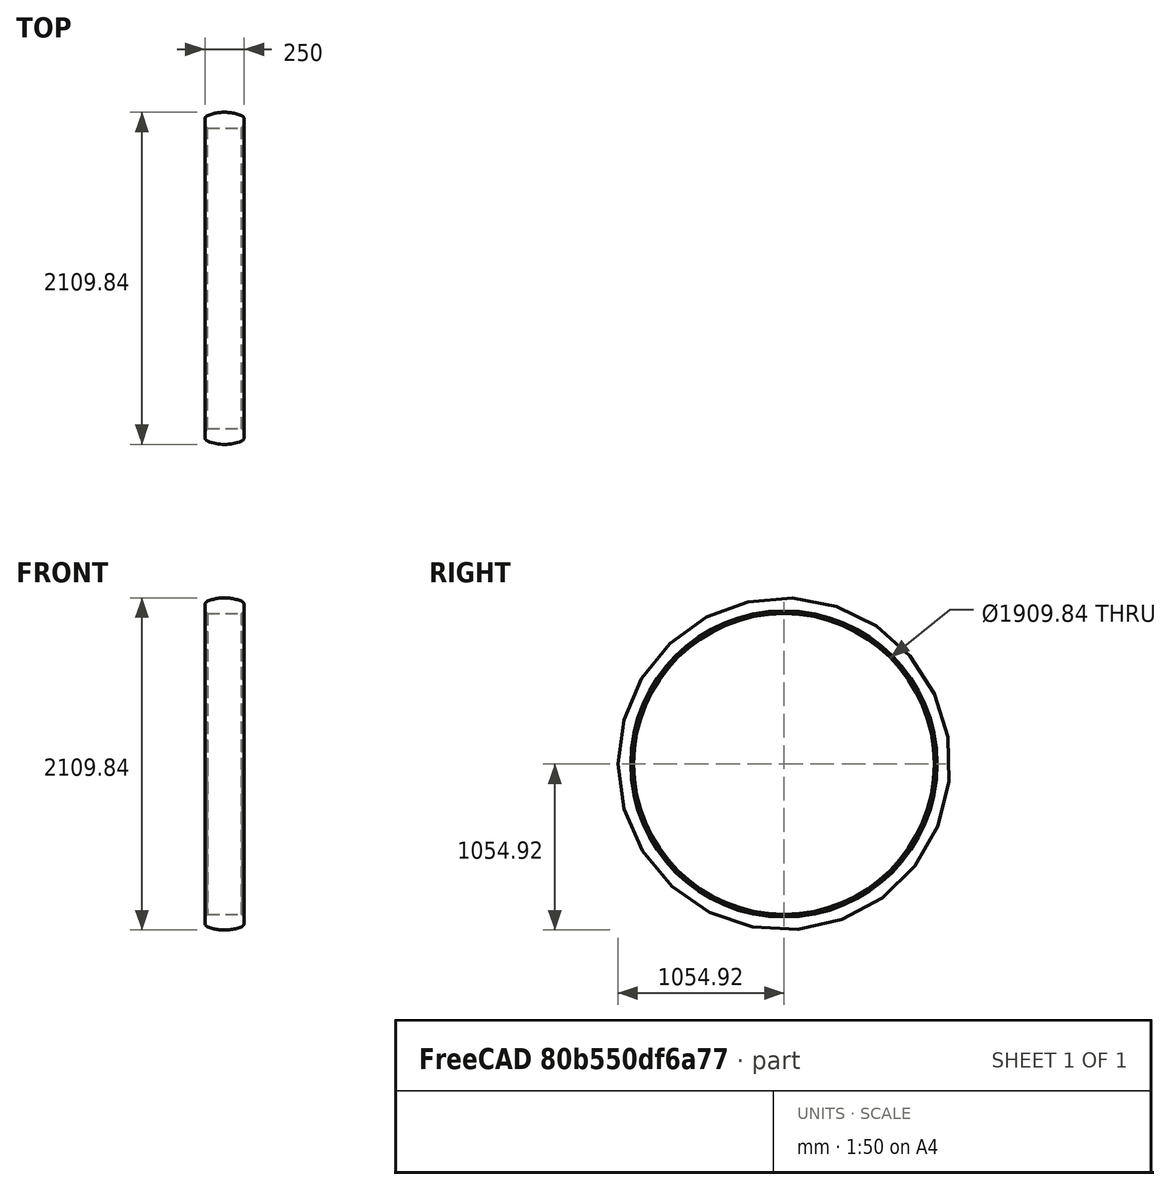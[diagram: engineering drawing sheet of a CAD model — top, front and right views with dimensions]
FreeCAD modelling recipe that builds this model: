
FCSTD DOCUMENT
Label: PR_014
objects: Sketcher::SketchObject×1, PartDesign::Revolution×1
note: 3 computed .brp shape members not serialized (recipe doc carries the construction recipe); baked Part::Feature solids carry a one-line shape summary decoded from their .brp

FEATURE [Sketcher::SketchObject] Sketch
  sketch-geometry (9):
    g0: LineSegment StartX=17.6777 StartY=-954.92 StartZ=0 EndX=232.322 EndY=-954.92 EndZ=0
    g1: LineSegment StartX=0 StartY=-972.598 StartZ=0 EndX=0 EndY=-1008.23 EndZ=0
    g2: LineSegment StartX=17.6777 StartY=-954.92 StartZ=0 EndX=0 EndY=-972.598 EndZ=0
    g3: LineSegment StartX=232.322 StartY=-954.92 StartZ=0 EndX=250 EndY=-972.598 EndZ=0
    g4: LineSegment StartX=250 StartY=-1008.23 StartZ=0 EndX=250 EndY=-972.598 EndZ=0
    g5: ArcOfCircle CenterX=28 CenterY=-1008.23 CenterZ=0 NormalX=0 NormalY=0 NormalZ=1 Radius=28 StartAngle=3.14159 EndAngle=4.33161
    g6: ArcOfCircle CenterX=222 CenterY=-1008.23 CenterZ=0 NormalX=0 NormalY=0 NormalZ=1 Radius=28 StartAngle=5.09317 EndAngle=6.28319
    g7: ArcOfCircle CenterX=125 CenterY=-765.92 CenterZ=0 NormalX=0 NormalY=0 NormalZ=1 Radius=289 StartAngle=4.33161 EndAngle=5.09317
    g8: LineSegment [constr] StartX=21.3562 StartY=-1054.92 StartZ=0 EndX=437.798 EndY=-1054.92 EndZ=0
  constraints (27):
    c: Horizontal(g0)
    c: DistanceY(g0) = -954.92
    c: Vertical(g1)
    c: Coincident(g2,g0)
    c: Coincident(g2,g1)
    c: Coincident(g3,g0)
    c: Vertical(g4)
    c: Coincident(g3,g4)
    c: DistanceX(g1) = 0
    c: Angle(g1,g2) = 2.35619
    c: Angle(g3,g4) = 2.35619
    c: DistanceX(g1,g3) = 250
    c: Distance(g2) = 25
    c: Distance(g3) = 25
    c: Radius(g5) = 28
    c: Radius(g6) = 28
    c: Radius(g7) = 289
    c: Tangent(g1,g5)
    c: Tangent(g5,g7)
    c: Tangent(g7,g6)
    c: Tangent(g6,g4)
    c: Horizontal(g8)
    c: Tangent(g8,g7)
    c: DistanceY(g8,g0) = 100
    c: DistanceX(g7) = 125
    c: DistanceX(g8) = 21.3562
    c: Distance(g8) = 416.442
FEATURE [PartDesign::Revolution] Revolution
  Angle = 360
  Axis = (1,0,0)
  Base = (0,0,0)
  ReferenceAxis = -> Sketch [H_Axis]
  Sketch = -> Sketch
